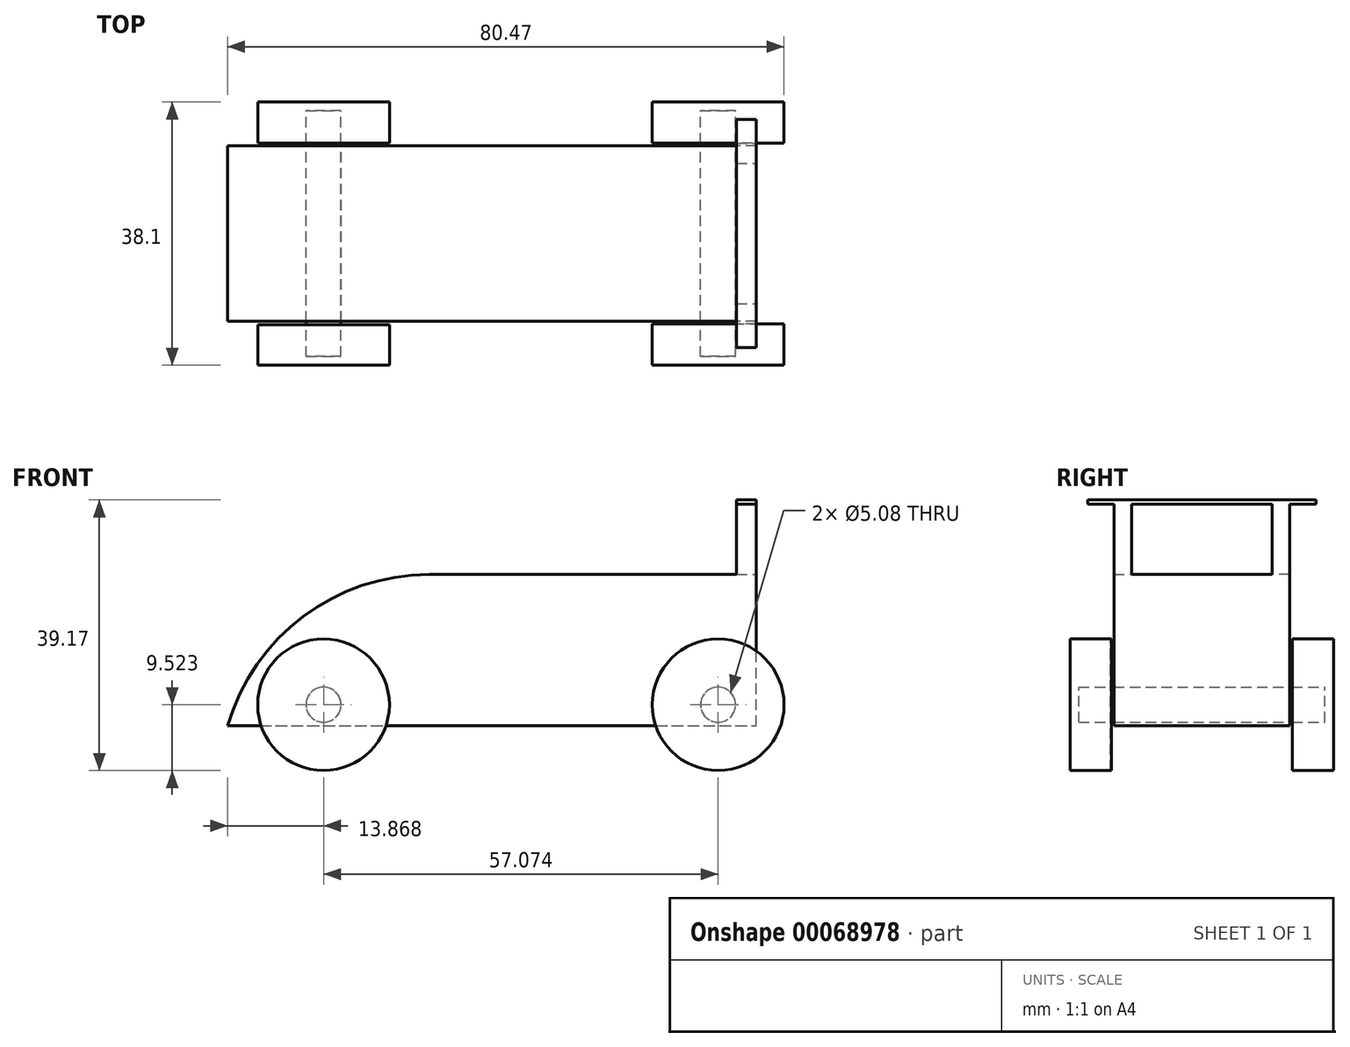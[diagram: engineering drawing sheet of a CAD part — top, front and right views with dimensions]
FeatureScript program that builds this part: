
annotation { "Feature Type Name" : "Feature", "Feature Type Description" : "" }
export const myFeature = defineFeature(function(context is Context, id is Id, definition is map)
    precondition{}
    {
        {
            var Q0;
            Q0=qCreatedBy(makeId("Front.planeOp"),FACE);
            var sketch = newSketch(context, id + "F0", { "sketchPlane" : qUnion([Q0])});
            skLineSegment(sketch, "E0", {"start": v(0, 0) * mm, "end": v(76.44, 0) * mm});
            skLineSegment(sketch, "E1", {"start": v(76.44, 0) * mm, "end": v(76.44, 21.9) * mm});
            skLineSegment(sketch, "E2", {"start": v(76.44, 21.9) * mm, "end": v(29.14, 21.9) * mm});
            skArc(sketch, "E3", {"start": v(29.14, 21.9) * mm, "mid": v(10.92, 15.82) * mm, "end": v(0, 0) * mm});
            skSolve(sketch);
        }
        {
            var Q0;
            Q0 = qSketchRegion(id + "F0", true);
            extrude(context, id + "F1", {"entities" : qUnion([Q0]), "depth" : 25.4 * mm});
        }
        {
            var Q0;
            Q0=qCreatedBy(makeId("Front.planeOp"),FACE);
            var sketch = newSketch(context, id + "F2", { "sketchPlane" : qUnion([Q0])});
            skCircle(sketch, "E4", {"center": v(13.87, 3.05) * mm, "radius": 1.9 * mm});
            skCircle(sketch, "E5", {"center": v(70.94, 3.05) * mm, "radius": 1.9 * mm});
            skSolve(sketch);
        }
        {
            var Q0;
            Q0=sQuery(id+"F2.wireOp",VERTEX,"E4.center");
            var Q1;
            Q1=sQuery(id+"F2.wireOp",VERTEX,"E5.center");
            var Q2;
            Q2=makeQuery(id+"F1.opExtrude","SWEPT_BODY",BODY,{"disambiguationData":[OSD([sQuery(id+"F0.wireOp",EDGE,"E0"),sQuery(id+"F0.wireOp",EDGE,"E1"),sQuery(id+"F0.wireOp",EDGE,"E2"),sQuery(id+"F0.wireOp",EDGE,"E3")])]});
            hole(context, id + "F3", {"style" : HoleStyle.SIMPLE, "holeDiameter" : 5.08 * mm, "endStyle" : HoleEndStyle.THROUGH, "oppositeDirection" : true, "locations" : qUnion([Q0, Q1]), "scope" : qUnion([Q2])});
        }
        {
            var Q0;
            Q0=makeQuery(id+"F1.opExtrude","CAP_FACE",FACE,{"disambiguationData":[OSD([sQuery(id+"F0.wireOp",EDGE,"E0"),sQuery(id+"F0.wireOp",EDGE,"E1"),sQuery(id+"F0.wireOp",EDGE,"E2"),sQuery(id+"F0.wireOp",EDGE,"E3")])],"isStart":false});
            var sketch = newSketch(context, id + "F4", { "sketchPlane" : qUnion([Q0])});
            skCircle(sketch, "E6", {"center": v(13.87, 3.05) * mm, "radius": 2.54 * mm});
            skCircle(sketch, "E7", {"center": v(70.94, 3.05) * mm, "radius": 2.53 * mm});
            skSolve(sketch);
        }
        {
            var Q0;
            Q0=makeQuery(id+"F4.imprint","IMPRINT",FACE,{"disambiguationData":[TD([[makeQuery(id+"F4.imprint","IMPRINT",EDGE,{"derivedFrom":sQuery(id+"F4.wireOp",EDGE,"E6")}),1.0]])]});
            extrude(context, id + "F5", {"entities" : qUnion([Q0]), "depth" : 5.08 * mm, "hasSecondDirection" : true, "secondDirectionOppositeDirection" : true, "secondDirectionDepth" : 30.48 * mm});
        }
        {
            var Q0;
            Q0=makeQuery(id+"F1.opExtrude","CAP_FACE",FACE,{"disambiguationData":[OSD([sQuery(id+"F0.wireOp",EDGE,"E0"),sQuery(id+"F0.wireOp",EDGE,"E1"),sQuery(id+"F0.wireOp",EDGE,"E2"),sQuery(id+"F0.wireOp",EDGE,"E3")])],"isStart":false});
            var sketch = newSketch(context, id + "F6", { "sketchPlane" : qUnion([Q0])});
            skCircle(sketch, "E8", {"center": v(70.94, 3.05) * mm, "radius": 2.53 * mm});
            skSolve(sketch);
        }
        {
            var Q0;
            Q0 = qSketchRegion(id + "F6", true);
            extrude(context, id + "F7", {"entities" : qUnion([Q0]), "depth" : 5.08 * mm, "hasSecondDirection" : true, "secondDirectionOppositeDirection" : true, "secondDirectionDepth" : 30.48 * mm});
        }
        {
            var Q0;
            Q0=makeQuery(id+"F5.opExtrude","CAP_FACE",FACE,{"disambiguationData":[OSD([sQuery(id+"F4.wireOp",EDGE,"E6")])],"isStart":false});
            var sketch = newSketch(context, id + "F8", { "sketchPlane" : qUnion([Q0])});
            skCircle(sketch, "E9", {"center": v(13.87, 3.05) * mm, "radius": 9.53 * mm});
            skSolve(sketch);
        }
        {
            var Q0;
            Q0 = qSketchRegion(id + "F8", true);
            extrude(context, id + "F9", {"entities" : qUnion([Q0]), "depth" : 1.27 * mm, "hasSecondDirection" : true, "secondDirectionOppositeDirection" : true, "secondDirectionDepth" : 4.57 * mm});
        }
        {
            var Q0;
            Q0=makeQuery(id+"F7.opExtrude","CAP_FACE",FACE,{"disambiguationData":[OSD([sQuery(id+"F6.wireOp",EDGE,"E8")])],"isStart":false});
            var sketch = newSketch(context, id + "F10", { "sketchPlane" : qUnion([Q0])});
            skCircle(sketch, "E10", {"center": v(70.94, 3.05) * mm, "radius": 9.53 * mm});
            skSolve(sketch);
        }
        {
            var Q0;
            Q0 = qSketchRegion(id + "F10", true);
            extrude(context, id + "F11", {"entities" : qUnion([Q0]), "depth" : 1.27 * mm, "hasSecondDirection" : true, "secondDirectionOppositeDirection" : true, "secondDirectionDepth" : 4.7 * mm});
        }
        {
            var Q0;
            Q0=makeQuery(id+"F7.opExtrude","CAP_FACE",FACE,{"disambiguationData":[OSD([sQuery(id+"F6.wireOp",EDGE,"E8")])],"isStart":true});
            var sketch = newSketch(context, id + "F12", { "sketchPlane" : qUnion([Q0])});
            skCircle(sketch, "E11", {"center": v(-70.94, 3.05) * mm, "radius": 9.53 * mm});
            skSolve(sketch);
        }
        {
            var Q0;
            Q0 = qSketchRegion(id + "F12", true);
            extrude(context, id + "F13", {"entities" : qUnion([Q0]), "depth" : 1.27 * mm, "hasSecondDirection" : true, "secondDirectionOppositeDirection" : true, "secondDirectionDepth" : 4.7 * mm});
        }
        {
            var Q0;
            Q0=makeQuery(id+"F5.opExtrude","CAP_FACE",FACE,{"disambiguationData":[OSD([sQuery(id+"F4.wireOp",EDGE,"E6")])],"isStart":true});
            var sketch = newSketch(context, id + "F14", { "sketchPlane" : qUnion([Q0])});
            skCircle(sketch, "E12", {"center": v(-13.87, 3.05) * mm, "radius": 9.53 * mm});
            skSolve(sketch);
        }
        {
            var Q0;
            Q0 = qSketchRegion(id + "F14", true);
            extrude(context, id + "F15", {"entities" : qUnion([Q0]), "depth" : 1.27 * mm, "hasSecondDirection" : true, "secondDirectionOppositeDirection" : true, "secondDirectionDepth" : 4.7 * mm});
        }
        {
            var Q0;
            Q0=makeQuery(id+"F1.opExtrude","SWEPT_FACE",FACE,{"disambiguationData":[OSD([sQuery(id+"F0.wireOp",EDGE,"E2")])]});
            var sketch = newSketch(context, id + "F16", { "sketchPlane" : qUnion([Q0])});
            skLineSegment(sketch, "E13", {"start": v(76.44, -25.4) * mm, "end": v(76.44, 0) * mm});
            skLineSegment(sketch, "E14", {"start": v(76.44, 0) * mm, "end": v(73.62, 0) * mm});
            skLineSegment(sketch, "E15", {"start": v(73.62, 0) * mm, "end": v(73.62, -25.4) * mm});
            skLineSegment(sketch, "E16", {"start": v(73.62, -25.4) * mm, "end": v(76.44, -25.4) * mm});
            skLineSegment(sketch, "E17", {"start": v(73.62, -22.86) * mm, "end": v(76.44, -22.86) * mm});
            skLineSegment(sketch, "E18", {"start": v(73.62, -2.54) * mm, "end": v(76.44, -2.54) * mm});
            skSolve(sketch);
        }
        {
            var Q0;
            {var subQ0=sQuery(id+"F16.wireOp",EDGE,"E16");Q0=makeQuery(id+"F16.imprint","IMPRINT",FACE,{"disambiguationData":[TD([[makeQuery(id+"F16.imprint","IMPRINT",EDGE,{"derivedFrom":subQ0}),-1.0]])]});}
            var Q1;
            {var subQ0=sQuery(id+"F16.wireOp",EDGE,"E14");Q1=makeQuery(id+"F16.imprint","IMPRINT",FACE,{"disambiguationData":[TD([[makeQuery(id+"F16.imprint","IMPRINT",EDGE,{"derivedFrom":subQ0}),1.0]])]});}
            extrude(context, id + "F17", {"entities" : qUnion([Q0, Q1]), "operationType" : NewBodyOperationType.ADD, "depth" : 10.16 * mm});
        }
        {
            var Q0;
            Q0=makeQuery(id+"F17.opExtrude","CAP_FACE",FACE,{"disambiguationData":[OSD([sQuery(id+"F16.wireOp",EDGE,"E13"),sQuery(id+"F16.wireOp",EDGE,"E15"),sQuery(id+"F16.wireOp",EDGE,"E16"),sQuery(id+"F16.wireOp",EDGE,"E17")])],"isStart":false});
            var sketch = newSketch(context, id + "F18", { "sketchPlane" : qUnion([Q0])});
            skLineSegment(sketch, "E19", {"start": v(73.62, -25.4) * mm, "end": v(73.62, 0) * mm});
            skLineSegment(sketch, "E20", {"start": v(73.62, 0) * mm, "end": v(76.44, 0) * mm});
            skLineSegment(sketch, "E21", {"start": v(76.44, 0) * mm, "end": v(76.44, -25.4) * mm});
            skLineSegment(sketch, "E22", {"start": v(76.44, -25.4) * mm, "end": v(73.62, -25.4) * mm});
            skLineSegment(sketch, "E23", {"start": v(73.62, -25.4) * mm, "end": v(73.62, -29.21) * mm});
            skLineSegment(sketch, "E24", {"start": v(73.62, 0) * mm, "end": v(73.62, 3.81) * mm});
            skLineSegment(sketch, "E25", {"start": v(73.62, -29.21) * mm, "end": v(76.44, -29.21) * mm});
            skLineSegment(sketch, "E26", {"start": v(76.44, -29.21) * mm, "end": v(76.44, -25.4) * mm});
            skLineSegment(sketch, "E27", {"start": v(76.44, 0) * mm, "end": v(76.44, 3.81) * mm});
            skLineSegment(sketch, "E28", {"start": v(76.44, 3.81) * mm, "end": v(73.62, 3.81) * mm});
            skSolve(sketch);
        }
        {
            var Q0;
            Q0 = qSketchRegion(id + "F18", true);
            extrude(context, id + "F19", {"entities" : qUnion([Q0]), "operationType" : NewBodyOperationType.ADD, "depth" : 0.64 * mm});
        }
    });
